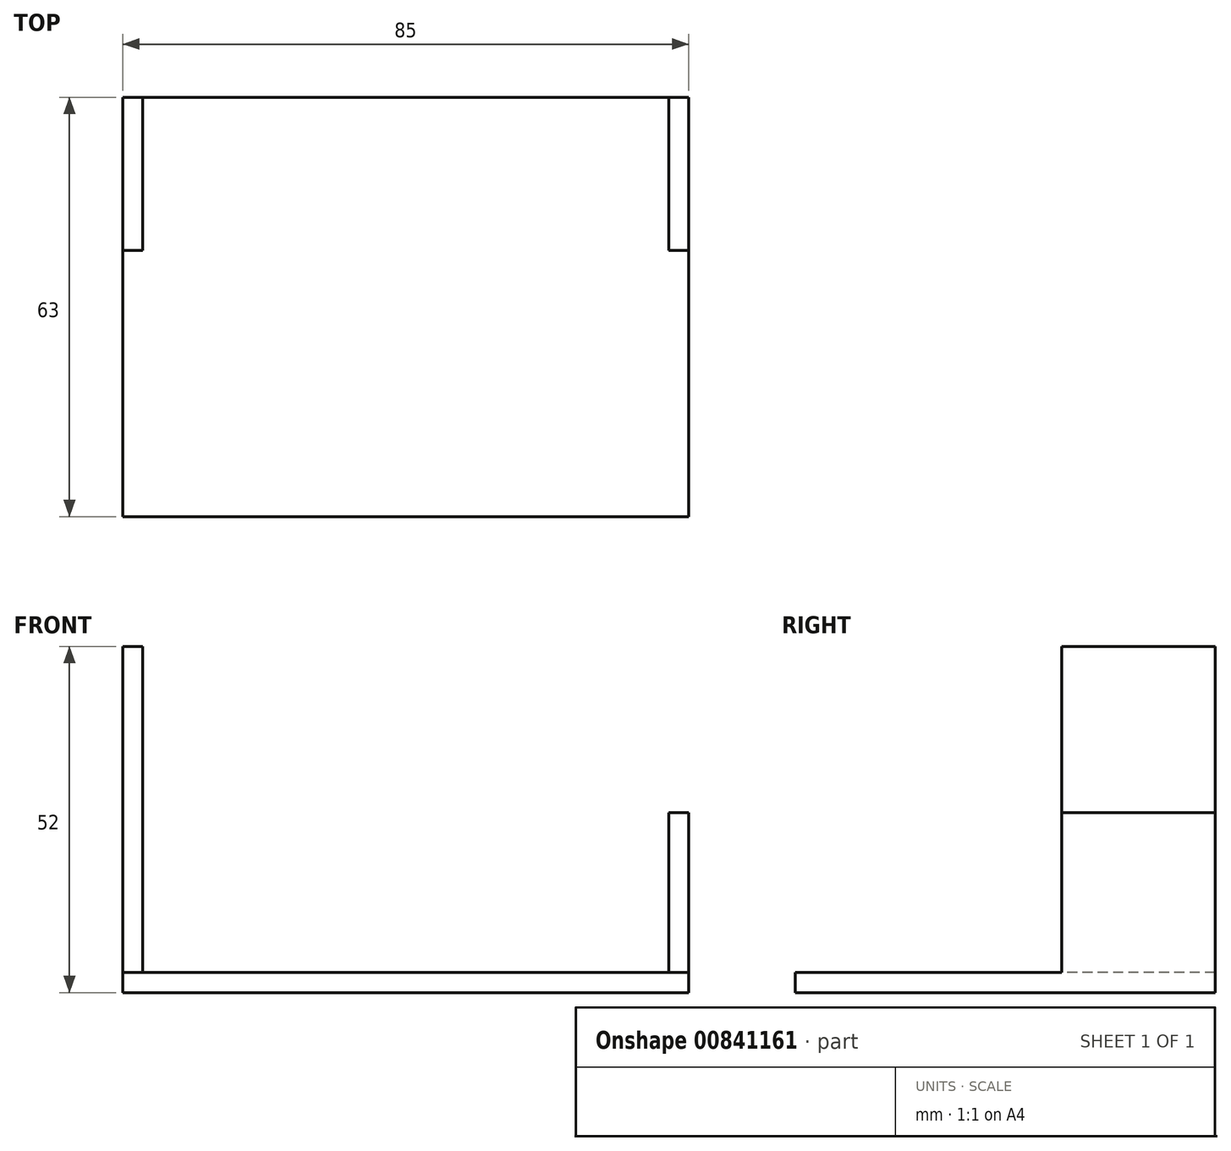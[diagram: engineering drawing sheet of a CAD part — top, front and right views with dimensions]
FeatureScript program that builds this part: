
annotation { "Feature Type Name" : "Feature", "Feature Type Description" : "" }
export const myFeature = defineFeature(function(context is Context, id is Id, definition is map)
    precondition{}
    {
        {
            var Q0;
            Q0=qCreatedBy(makeId("Top.planeOp"),FACE);
            var sketch = newSketch(context, id + "F0", { "sketchPlane" : qUnion([Q0])});
            skLineSegment(sketch, "E0.bottom", {"start": v(0, 0) * mm, "end": v(85, 0) * mm});
            skLineSegment(sketch, "E0.top", {"start": v(0, 23) * mm, "end": v(85, 23) * mm});
            skLineSegment(sketch, "E0.left", {"start": v(0, 0) * mm, "end": v(0, 23) * mm});
            skLineSegment(sketch, "E0.right", {"start": v(85, 0) * mm, "end": v(85, 23) * mm});
            skLineSegment(sketch, "E1.top", {"start": v(0, -40) * mm, "end": v(85, -40) * mm});
            skLineSegment(sketch, "E1.left", {"start": v(0, 0) * mm, "end": v(0, -40) * mm});
            skLineSegment(sketch, "E1.right", {"start": v(85, 0) * mm, "end": v(85, -40) * mm});
            skSolve(sketch);
        }
        {
            var Q0;
            Q0=qSketchRegion(id+"F0",true);
            extrude(context, id + "F1", {"entities" : qUnion([Q0]), "depth" : 3 * mm, "offsetDistance" : 25 * mm});
        }
        {
            var Q0;
            Q0=makeQuery(id+"F1.opExtrude","CAP_FACE",FACE,{"disambiguationData":[OSD([sQuery(id+"F0.wireOp",EDGE,"E0.bottom"),sQuery(id+"F0.wireOp",EDGE,"E0.top"),sQuery(id+"F0.wireOp",EDGE,"E0.left"),sQuery(id+"F0.wireOp",EDGE,"E0.right")])],"isStart":false});
            var sketch = newSketch(context, id + "F2", { "sketchPlane" : qUnion([Q0])});
            skLineSegment(sketch, "E2.bottom", {"start": v(0, 23) * mm, "end": v(3, 23) * mm});
            skLineSegment(sketch, "E2.top", {"start": v(0, 0) * mm, "end": v(3, 0) * mm});
            skLineSegment(sketch, "E2.left", {"start": v(0, 23) * mm, "end": v(0, 0) * mm});
            skLineSegment(sketch, "E2.right", {"start": v(3, 23) * mm, "end": v(3, 0) * mm});
            skLineSegment(sketch, "E3.bottom", {"start": v(85, 23) * mm, "end": v(82, 23) * mm});
            skLineSegment(sketch, "E3.top", {"start": v(85, 0) * mm, "end": v(82, 0) * mm});
            skLineSegment(sketch, "E3.left", {"start": v(85, 23) * mm, "end": v(85, 0) * mm});
            skLineSegment(sketch, "E3.right", {"start": v(82, 23) * mm, "end": v(82, 0) * mm});
            skSolve(sketch);
        }
        {
            var Q0;
            Q0=qSketchRegion(id+"F2",true);
            extrude(context, id + "F3", {"entities" : qUnion([Q0]), "operationType" : NewBodyOperationType.ADD, "depth" : 24 * mm, "offsetDistance" : 25 * mm});
        }
        {
            var Q0;
            Q0=makeQuery(id+"F3.opExtrude","CAP_FACE",FACE,{"disambiguationData":[OSD([sQuery(id+"F2.wireOp",EDGE,"E2.bottom"),sQuery(id+"F2.wireOp",EDGE,"E2.top"),sQuery(id+"F2.wireOp",EDGE,"E2.left"),sQuery(id+"F2.wireOp",EDGE,"E2.right")])],"isStart":false});
            var sketch = newSketch(context, id + "F4", { "sketchPlane" : qUnion([Q0])});
            skLineSegment(sketch, "E4.bottom", {"start": v(0, 23) * mm, "end": v(3, 23) * mm});
            skLineSegment(sketch, "E4.top", {"start": v(0, 0) * mm, "end": v(3, 0) * mm});
            skLineSegment(sketch, "E4.left", {"start": v(0, 23) * mm, "end": v(0, 0) * mm});
            skLineSegment(sketch, "E4.right", {"start": v(3, 23) * mm, "end": v(3, 0) * mm});
            skSolve(sketch);
        }
        {
            var Q0;
            Q0=qSketchRegion(id+"F4",true);
            extrude(context, id + "F5", {"entities" : qUnion([Q0]), "operationType" : NewBodyOperationType.ADD, "depth" : 25 * mm, "offsetDistance" : 25 * mm});
        }
    });
